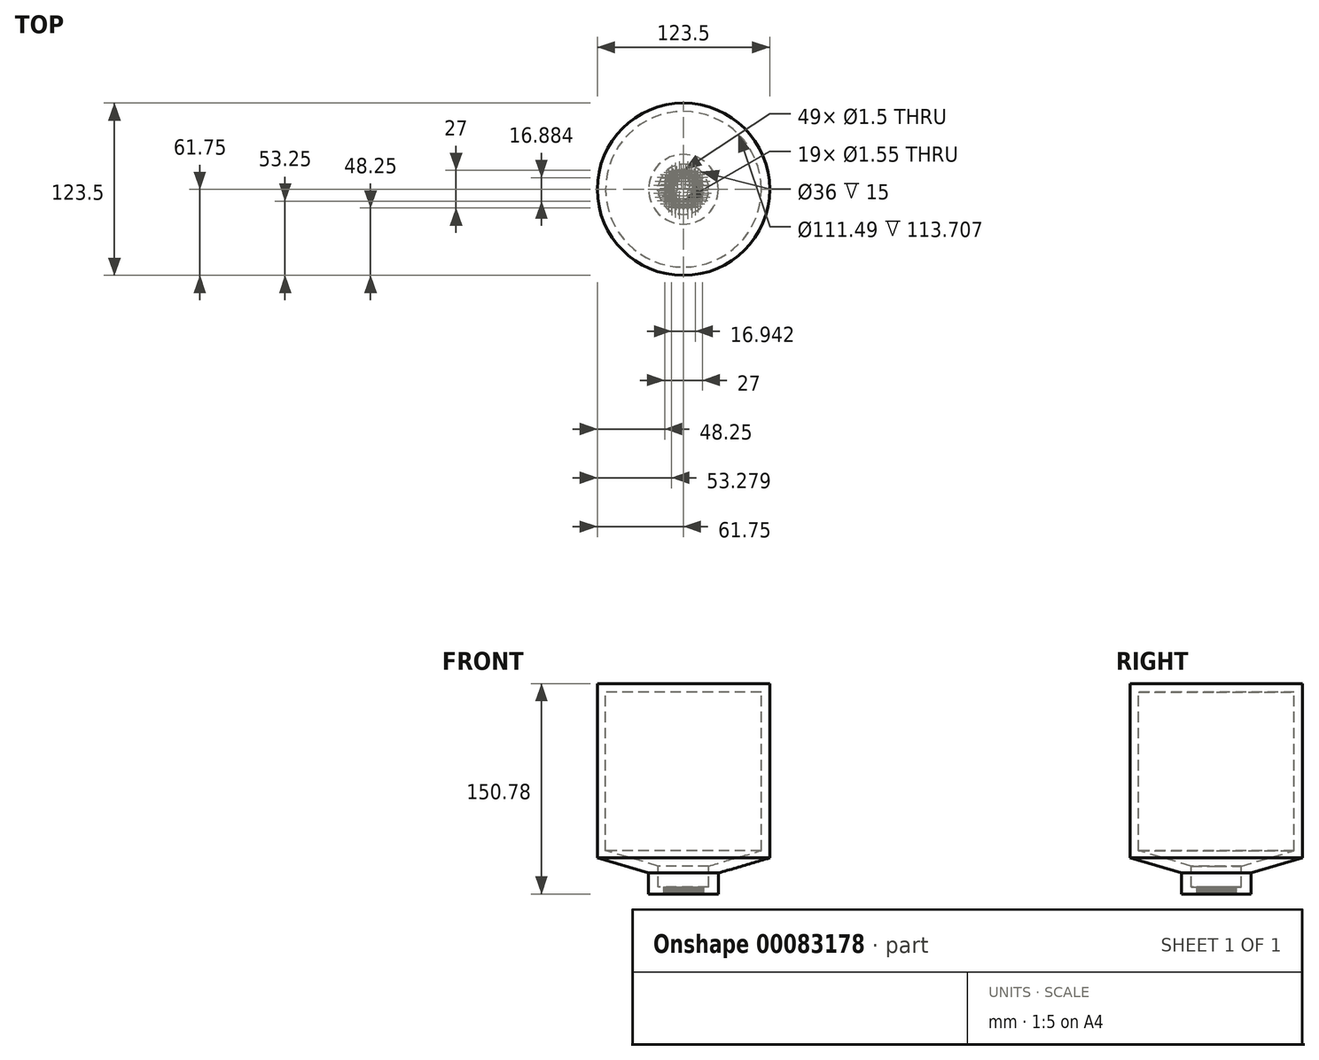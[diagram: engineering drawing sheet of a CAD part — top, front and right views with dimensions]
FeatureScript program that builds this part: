
annotation { "Feature Type Name" : "Feature", "Feature Type Description" : "" }
export const myFeature = defineFeature(function(context is Context, id is Id, definition is map)
    precondition{}
    {
        {
            var Q0;
            Q0=qCreatedBy(makeId("Front.planeOp"),FACE);
            var sketch = newSketch(context, id + "F0", { "sketchPlane" : qUnion([Q0])});
            skLineSegment(sketch, "E0", {"start": v(0, 60.78) * mm, "end": v(0, -41.7) * mm, "construction": true});
            skLineSegment(sketch, "E1", {"start": v(0, 0) * mm, "end": v(-25, 0) * mm});
            skLineSegment(sketch, "E2", {"start": v(-25, 0) * mm, "end": v(-25, 15) * mm});
            skLineSegment(sketch, "E3", {"start": v(-25, 15) * mm, "end": v(-61.75, 25.78) * mm});
            skLineSegment(sketch, "E4", {"start": v(-61.75, 25.78) * mm, "end": v(-61.75, 150.78) * mm});
            skLineSegment(sketch, "E5", {"start": v(-61.75, 150.78) * mm, "end": v(0, 150.78) * mm});
            skLineSegment(sketch, "E6", {"start": v(0, 150.78) * mm, "end": v(0, 144.78) * mm});
            skLineSegment(sketch, "E7", {"start": v(0, 144.78) * mm, "end": v(-55.75, 144.78) * mm});
            skLineSegment(sketch, "E8", {"start": v(-55.75, 144.78) * mm, "end": v(-55.75, 31.07) * mm});
            skLineSegment(sketch, "E9", {"start": v(-55.75, 31.07) * mm, "end": v(-18, 20) * mm});
            skLineSegment(sketch, "E10", {"start": v(-18, 20) * mm, "end": v(-18, 5) * mm});
            skLineSegment(sketch, "E11", {"start": v(-18, 5) * mm, "end": v(0, 5) * mm});
            skLineSegment(sketch, "E12", {"start": v(0, 0) * mm, "end": v(0, 5) * mm});
            skSolve(sketch);
        }
        {
            var Q0;
            Q0=makeQuery(id+"F0.imprint","IMPRINT",FACE,{"disambiguationData":[TD([[makeQuery(id+"F0.imprint","IMPRINT",EDGE,{"derivedFrom":sQuery(id+"F0.wireOp",EDGE,"E1")}),-1.0]])]});
            var Q1;
            Q1=sQuery(id+"F0.wireOp",EDGE,"E0");
            revolve(context, id + "F1", {"entities" : qUnion([Q0]), "axis" : qUnion([Q1]), "revolveType" : RevolveType.FULL});
        }
        {
            var Q0;
            Q0=qCreatedBy(makeId("Top.planeOp"),FACE);
            var sketch = newSketch(context, id + "F2", { "sketchPlane" : qUnion([Q0])});
            skCircle(sketch, "E13", {"center": v(0, 0) * mm, "radius": 11 * mm, "construction": true});
            skCircle(sketch, "E14", {"center": v(0, 0) * mm, "radius": 13.5 * mm, "construction": true});
            skCircle(sketch, "E15", {"center": v(0, -13.5) * mm, "radius": 0.75 * mm});
            skCircle(sketch, "E16.1.0", {"center": v(3, -13.16) * mm, "radius": 0.75 * mm});
            skCircle(sketch, "E16.2.0", {"center": v(5.86, -12.16) * mm, "radius": 0.75 * mm});
            skCircle(sketch, "E17.1.3.0", {"center": v(8.42, -10.55) * mm, "radius": 0.75 * mm});
            skCircle(sketch, "E17.1.4.0", {"center": v(10.55, -8.42) * mm, "radius": 0.75 * mm});
            skCircle(sketch, "E17.1.5.0", {"center": v(12.16, -5.86) * mm, "radius": 0.75 * mm});
            skCircle(sketch, "E17.1.6.0", {"center": v(13.16, -3) * mm, "radius": 0.75 * mm});
            skCircle(sketch, "E17.1.7.0", {"center": v(13.5, 0) * mm, "radius": 0.75 * mm});
            skCircle(sketch, "E17.1.8.0", {"center": v(13.16, 3) * mm, "radius": 0.75 * mm});
            skCircle(sketch, "E17.1.9.0", {"center": v(12.16, 5.86) * mm, "radius": 0.75 * mm});
            skCircle(sketch, "E17.1.10.0", {"center": v(10.55, 8.42) * mm, "radius": 0.75 * mm});
            skCircle(sketch, "E17.1.11.0", {"center": v(8.42, 10.55) * mm, "radius": 0.75 * mm});
            skCircle(sketch, "E17.1.12.0", {"center": v(5.86, 12.16) * mm, "radius": 0.75 * mm});
            skCircle(sketch, "E17.1.13.0", {"center": v(3, 13.16) * mm, "radius": 0.75 * mm});
            skCircle(sketch, "E17.1.14.0", {"center": v(0, 13.5) * mm, "radius": 0.75 * mm});
            skCircle(sketch, "E17.1.15.0", {"center": v(-3, 13.16) * mm, "radius": 0.75 * mm});
            skCircle(sketch, "E17.1.16.0", {"center": v(-5.86, 12.16) * mm, "radius": 0.75 * mm});
            skCircle(sketch, "E17.1.17.0", {"center": v(-8.42, 10.55) * mm, "radius": 0.75 * mm});
            skCircle(sketch, "E17.1.18.0", {"center": v(-10.55, 8.42) * mm, "radius": 0.75 * mm});
            skCircle(sketch, "E17.1.19.0", {"center": v(-12.16, 5.86) * mm, "radius": 0.75 * mm});
            skCircle(sketch, "E17.1.20.0", {"center": v(-13.16, 3) * mm, "radius": 0.75 * mm});
            skCircle(sketch, "E17.1.21.0", {"center": v(-13.5, 0) * mm, "radius": 0.75 * mm});
            skCircle(sketch, "E17.1.22.0", {"center": v(-13.16, -3) * mm, "radius": 0.75 * mm});
            skCircle(sketch, "E17.1.23.0", {"center": v(-12.16, -5.86) * mm, "radius": 0.75 * mm});
            skCircle(sketch, "E17.1.24.0", {"center": v(-10.55, -8.42) * mm, "radius": 0.75 * mm});
            skCircle(sketch, "E18.1.25.0", {"center": v(-8.42, -10.55) * mm, "radius": 0.75 * mm});
            skCircle(sketch, "E18.1.26.0", {"center": v(-5.86, -12.16) * mm, "radius": 0.75 * mm});
            skCircle(sketch, "E19.1.27.0", {"center": v(-3, -13.16) * mm, "radius": 0.75 * mm});
            skCircle(sketch, "E20", {"center": v(0, -11) * mm, "radius": 0.75 * mm});
            skCircle(sketch, "E21.1.0", {"center": v(3.24, -10.51) * mm, "radius": 0.75 * mm});
            skCircle(sketch, "E21.2.0", {"center": v(6.2, -9.09) * mm, "radius": 0.75 * mm});
            skCircle(sketch, "E21.3.0", {"center": v(8.6, -6.86) * mm, "radius": 0.75 * mm});
            skCircle(sketch, "E21.4.0", {"center": v(10.24, -4.02) * mm, "radius": 0.75 * mm});
            skCircle(sketch, "E21.5.0", {"center": v(10.97, -0.82) * mm, "radius": 0.75 * mm});
            skCircle(sketch, "E21.6.0", {"center": v(10.72, 2.45) * mm, "radius": 0.75 * mm});
            skCircle(sketch, "E21.7.0", {"center": v(9.53, 5.5) * mm, "radius": 0.75 * mm});
            skCircle(sketch, "E21.8.0", {"center": v(7.48, 8.06) * mm, "radius": 0.75 * mm});
            skCircle(sketch, "E21.9.0", {"center": v(4.77, 9.91) * mm, "radius": 0.75 * mm});
            skCircle(sketch, "E21.10.0", {"center": v(1.64, 10.88) * mm, "radius": 0.75 * mm});
            skCircle(sketch, "E21.11.0", {"center": v(-1.64, 10.88) * mm, "radius": 0.75 * mm});
            skCircle(sketch, "E21.12.0", {"center": v(-4.77, 9.91) * mm, "radius": 0.75 * mm});
            skCircle(sketch, "E21.13.0", {"center": v(-7.48, 8.06) * mm, "radius": 0.75 * mm});
            skCircle(sketch, "E21.14.0", {"center": v(-9.53, 5.5) * mm, "radius": 0.75 * mm});
            skCircle(sketch, "E21.15.0", {"center": v(-10.72, 2.45) * mm, "radius": 0.75 * mm});
            skCircle(sketch, "E21.16.0", {"center": v(-10.97, -0.82) * mm, "radius": 0.75 * mm});
            skCircle(sketch, "E21.17.0", {"center": v(-10.24, -4.02) * mm, "radius": 0.75 * mm});
            skCircle(sketch, "E21.18.0", {"center": v(-8.6, -6.86) * mm, "radius": 0.75 * mm});
            skCircle(sketch, "E21.19.0", {"center": v(-6.2, -9.09) * mm, "radius": 0.75 * mm});
            skCircle(sketch, "E21.20.0", {"center": v(-3.24, -10.51) * mm, "radius": 0.75 * mm});
            skCircle(sketch, "E22", {"center": v(0, 0) * mm, "radius": 8.5 * mm});
            skCircle(sketch, "E23", {"center": v(0, -8.5) * mm, "radius": 0.78 * mm});
            skCircle(sketch, "E24.1.0", {"center": v(2.76, -8.04) * mm, "radius": 0.78 * mm});
            skCircle(sketch, "E24.2.0", {"center": v(5.22, -6.7) * mm, "radius": 0.78 * mm});
            skCircle(sketch, "E24.3.0", {"center": v(7.12, -4.65) * mm, "radius": 0.78 * mm});
            skCircle(sketch, "E24.4.0", {"center": v(8.24, -2.09) * mm, "radius": 0.78 * mm});
            skCircle(sketch, "E24.5.0", {"center": v(8.47, 0.7) * mm, "radius": 0.78 * mm});
            skCircle(sketch, "E24.6.0", {"center": v(7.78, 3.41) * mm, "radius": 0.78 * mm});
            skCircle(sketch, "E24.7.0", {"center": v(6.25, 5.76) * mm, "radius": 0.78 * mm});
            skCircle(sketch, "E24.8.0", {"center": v(4.05, 7.48) * mm, "radius": 0.78 * mm});
            skCircle(sketch, "E24.9.0", {"center": v(1.4, 8.38) * mm, "radius": 0.78 * mm});
            skCircle(sketch, "E24.10.0", {"center": v(-1.4, 8.38) * mm, "radius": 0.78 * mm});
            skCircle(sketch, "E24.11.0", {"center": v(-4.05, 7.48) * mm, "radius": 0.78 * mm});
            skCircle(sketch, "E24.12.0", {"center": v(-6.25, 5.76) * mm, "radius": 0.78 * mm});
            skCircle(sketch, "E24.13.0", {"center": v(-7.78, 3.41) * mm, "radius": 0.78 * mm});
            skCircle(sketch, "E24.14.0", {"center": v(-8.47, 0.7) * mm, "radius": 0.78 * mm});
            skCircle(sketch, "E24.15.0", {"center": v(-8.24, -2.09) * mm, "radius": 0.78 * mm});
            skCircle(sketch, "E24.16.0", {"center": v(-7.12, -4.65) * mm, "radius": 0.78 * mm});
            skCircle(sketch, "E24.17.0", {"center": v(-5.22, -6.7) * mm, "radius": 0.78 * mm});
            skCircle(sketch, "E24.18.0", {"center": v(-2.76, -8.04) * mm, "radius": 0.78 * mm});
            skSolve(sketch);
        }
        {
            var Q0;
            Q0=makeQuery(id+"F2.imprint","IMPRINT",FACE,{"disambiguationData":[TD([[makeQuery(id+"F2.imprint","IMPRINT",EDGE,{"derivedFrom":sQuery(id+"F2.wireOp",EDGE,"E17.1.13.0")}),1.0]])]});
            var Q1;
            Q1=makeQuery(id+"F2.imprint","IMPRINT",FACE,{"disambiguationData":[TD([[makeQuery(id+"F2.imprint","IMPRINT",EDGE,{"derivedFrom":sQuery(id+"F2.wireOp",EDGE,"E17.1.14.0")}),1.0]])]});
            var Q2;
            Q2=makeQuery(id+"F2.imprint","IMPRINT",FACE,{"disambiguationData":[TD([[makeQuery(id+"F2.imprint","IMPRINT",EDGE,{"derivedFrom":sQuery(id+"F2.wireOp",EDGE,"E17.1.4.0")}),1.0]])]});
            var Q3;
            Q3=makeQuery(id+"F2.imprint","IMPRINT",FACE,{"disambiguationData":[TD([[makeQuery(id+"F2.imprint","IMPRINT",EDGE,{"derivedFrom":sQuery(id+"F2.wireOp",EDGE,"E17.1.5.0")}),1.0]])]});
            var Q4;
            Q4=makeQuery(id+"F2.imprint","IMPRINT",FACE,{"disambiguationData":[TD([[makeQuery(id+"F2.imprint","IMPRINT",EDGE,{"derivedFrom":sQuery(id+"F2.wireOp",EDGE,"E17.1.6.0")}),1.0]])]});
            var Q5;
            {var subQ0=sQuery(id+"F2.wireOp",EDGE,"E24.18.0");var subQ1=sQuery(id+"F2.wireOp",EDGE,"E22");var subQ2=makeQuery(id+"F2.imprint","INTERSECT",VERTEX,{"disambiguationData":[OD(0.0)],"derivedFrom":[subQ1,subQ0]});Q5=makeQuery(id+"F2.imprint","IMPRINT",FACE,{"disambiguationData":[TD([[makeQuery(id+"F2.imprint","IMPRINT",EDGE,{"disambiguationData":[TD([[subQ2,-1.0]])],"derivedFrom":subQ1}),1.0]])]});}
            var Q6;
            Q6=makeQuery(id+"F2.imprint","IMPRINT",FACE,{"disambiguationData":[TD([[makeQuery(id+"F2.imprint","IMPRINT",EDGE,{"derivedFrom":sQuery(id+"F2.wireOp",EDGE,"E21.11.0")}),1.0]])]});
            var Q7;
            Q7=makeQuery(id+"F2.imprint","IMPRINT",FACE,{"disambiguationData":[TD([[makeQuery(id+"F2.imprint","IMPRINT",EDGE,{"derivedFrom":sQuery(id+"F2.wireOp",EDGE,"E17.1.10.0")}),1.0]])]});
            var Q8;
            Q8=makeQuery(id+"F2.imprint","IMPRINT",FACE,{"disambiguationData":[TD([[makeQuery(id+"F2.imprint","IMPRINT",EDGE,{"derivedFrom":sQuery(id+"F2.wireOp",EDGE,"E17.1.9.0")}),1.0]])]});
            var Q9;
            Q9=makeQuery(id+"F2.imprint","IMPRINT",FACE,{"disambiguationData":[TD([[makeQuery(id+"F2.imprint","IMPRINT",EDGE,{"derivedFrom":sQuery(id+"F2.wireOp",EDGE,"E21.5.0")}),1.0]])]});
            var Q10;
            Q10=makeQuery(id+"F2.imprint","IMPRINT",FACE,{"disambiguationData":[TD([[makeQuery(id+"F2.imprint","IMPRINT",EDGE,{"derivedFrom":sQuery(id+"F2.wireOp",EDGE,"E17.1.11.0")}),1.0]])]});
            var Q11;
            Q11=makeQuery(id+"F2.imprint","IMPRINT",FACE,{"disambiguationData":[TD([[makeQuery(id+"F2.imprint","IMPRINT",EDGE,{"derivedFrom":sQuery(id+"F2.wireOp",EDGE,"E21.13.0")}),1.0]])]});
            var Q12;
            Q12=makeQuery(id+"F2.imprint","IMPRINT",FACE,{"disambiguationData":[TD([[makeQuery(id+"F2.imprint","IMPRINT",EDGE,{"derivedFrom":sQuery(id+"F2.wireOp",EDGE,"E17.1.12.0")}),1.0]])]});
            var Q13;
            Q13=makeQuery(id+"F2.imprint","IMPRINT",FACE,{"disambiguationData":[TD([[makeQuery(id+"F2.imprint","IMPRINT",EDGE,{"derivedFrom":sQuery(id+"F2.wireOp",EDGE,"E21.6.0")}),1.0]])]});
            var Q14;
            {var subQ0=sQuery(id+"F2.wireOp",EDGE,"E24.11.0");var subQ1=sQuery(id+"F2.wireOp",EDGE,"E22");var subQ2=makeQuery(id+"F2.imprint","INTERSECT",VERTEX,{"disambiguationData":[OD(0.0)],"derivedFrom":[subQ1,subQ0]});Q14=makeQuery(id+"F2.imprint","IMPRINT",FACE,{"disambiguationData":[TD([[makeQuery(id+"F2.imprint","IMPRINT",EDGE,{"disambiguationData":[TD([[subQ2,-1.0]])],"derivedFrom":subQ1}),-1.0]])]});}
            var Q15;
            Q15=makeQuery(id+"F2.imprint","IMPRINT",FACE,{"disambiguationData":[TD([[makeQuery(id+"F2.imprint","IMPRINT",EDGE,{"derivedFrom":sQuery(id+"F2.wireOp",EDGE,"E21.10.0")}),1.0]])]});
            var Q16;
            Q16=makeQuery(id+"F2.imprint","IMPRINT",FACE,{"disambiguationData":[TD([[makeQuery(id+"F2.imprint","IMPRINT",EDGE,{"derivedFrom":sQuery(id+"F2.wireOp",EDGE,"E16.1.0")}),1.0]])]});
            var Q17;
            Q17=makeQuery(id+"F2.imprint","IMPRINT",FACE,{"disambiguationData":[TD([[makeQuery(id+"F2.imprint","IMPRINT",EDGE,{"derivedFrom":sQuery(id+"F2.wireOp",EDGE,"E17.1.22.0")}),1.0]])]});
            var Q18;
            Q18=makeQuery(id+"F2.imprint","IMPRINT",FACE,{"disambiguationData":[TD([[makeQuery(id+"F2.imprint","IMPRINT",EDGE,{"derivedFrom":sQuery(id+"F2.wireOp",EDGE,"E21.7.0")}),1.0]])]});
            var Q19;
            Q19=makeQuery(id+"F2.imprint","IMPRINT",FACE,{"disambiguationData":[TD([[makeQuery(id+"F2.imprint","IMPRINT",EDGE,{"derivedFrom":sQuery(id+"F2.wireOp",EDGE,"E17.1.19.0")}),1.0]])]});
            var Q20;
            {var subQ0=sQuery(id+"F2.wireOp",EDGE,"E24.2.0");var subQ1=sQuery(id+"F2.wireOp",EDGE,"E22");var subQ2=makeQuery(id+"F2.imprint","INTERSECT",VERTEX,{"disambiguationData":[OD(0.0)],"derivedFrom":[subQ1,subQ0]});Q20=makeQuery(id+"F2.imprint","IMPRINT",FACE,{"disambiguationData":[TD([[makeQuery(id+"F2.imprint","IMPRINT",EDGE,{"disambiguationData":[TD([[subQ2,-1.0]])],"derivedFrom":subQ1}),1.0]])]});}
            var Q21;
            {var subQ0=sQuery(id+"F2.wireOp",EDGE,"E24.8.0");var subQ1=sQuery(id+"F2.wireOp",EDGE,"E22");var subQ2=makeQuery(id+"F2.imprint","INTERSECT",VERTEX,{"disambiguationData":[OD(0.0)],"derivedFrom":[subQ1,subQ0]});Q21=makeQuery(id+"F2.imprint","IMPRINT",FACE,{"disambiguationData":[TD([[makeQuery(id+"F2.imprint","IMPRINT",EDGE,{"disambiguationData":[TD([[subQ2,-1.0]])],"derivedFrom":subQ1}),-1.0]])]});}
            var Q22;
            Q22=makeQuery(id+"F2.imprint","IMPRINT",FACE,{"disambiguationData":[TD([[makeQuery(id+"F2.imprint","IMPRINT",EDGE,{"derivedFrom":sQuery(id+"F2.wireOp",EDGE,"E21.14.0")}),1.0]])]});
            var Q23;
            Q23=makeQuery(id+"F2.imprint","IMPRINT",FACE,{"disambiguationData":[TD([[makeQuery(id+"F2.imprint","IMPRINT",EDGE,{"derivedFrom":sQuery(id+"F2.wireOp",EDGE,"E17.1.20.0")}),1.0]])]});
            var Q24;
            {var subQ0=sQuery(id+"F2.wireOp",EDGE,"E24.15.0");var subQ1=sQuery(id+"F2.wireOp",EDGE,"E22");var subQ2=makeQuery(id+"F2.imprint","INTERSECT",VERTEX,{"disambiguationData":[OD(0.0)],"derivedFrom":[subQ1,subQ0]});Q24=makeQuery(id+"F2.imprint","IMPRINT",FACE,{"disambiguationData":[TD([[makeQuery(id+"F2.imprint","IMPRINT",EDGE,{"disambiguationData":[TD([[subQ2,-1.0]])],"derivedFrom":subQ1}),1.0]])]});}
            var Q25;
            Q25=makeQuery(id+"F2.imprint","IMPRINT",FACE,{"disambiguationData":[TD([[makeQuery(id+"F2.imprint","IMPRINT",EDGE,{"derivedFrom":sQuery(id+"F2.wireOp",EDGE,"E20")}),1.0]])]});
            var Q26;
            {var subQ0=sQuery(id+"F2.wireOp",EDGE,"E24.10.0");var subQ1=sQuery(id+"F2.wireOp",EDGE,"E22");var subQ2=makeQuery(id+"F2.imprint","INTERSECT",VERTEX,{"disambiguationData":[OD(0.0)],"derivedFrom":[subQ1,subQ0]});Q26=makeQuery(id+"F2.imprint","IMPRINT",FACE,{"disambiguationData":[TD([[makeQuery(id+"F2.imprint","IMPRINT",EDGE,{"disambiguationData":[TD([[subQ2,-1.0]])],"derivedFrom":subQ1}),-1.0]])]});}
            var Q27;
            {var subQ0=sQuery(id+"F2.wireOp",EDGE,"E24.4.0");var subQ1=sQuery(id+"F2.wireOp",EDGE,"E22");var subQ2=makeQuery(id+"F2.imprint","INTERSECT",VERTEX,{"disambiguationData":[OD(0.0)],"derivedFrom":[subQ1,subQ0]});Q27=makeQuery(id+"F2.imprint","IMPRINT",FACE,{"disambiguationData":[TD([[makeQuery(id+"F2.imprint","IMPRINT",EDGE,{"disambiguationData":[TD([[subQ2,-1.0]])],"derivedFrom":subQ1}),1.0]])]});}
            var Q28;
            Q28=makeQuery(id+"F2.imprint","IMPRINT",FACE,{"disambiguationData":[TD([[makeQuery(id+"F2.imprint","IMPRINT",EDGE,{"derivedFrom":sQuery(id+"F2.wireOp",EDGE,"E21.2.0")}),1.0]])]});
            var Q29;
            Q29=makeQuery(id+"F2.imprint","IMPRINT",FACE,{"disambiguationData":[TD([[makeQuery(id+"F2.imprint","IMPRINT",EDGE,{"derivedFrom":sQuery(id+"F2.wireOp",EDGE,"E21.9.0")}),1.0]])]});
            var Q30;
            Q30=makeQuery(id+"F2.imprint","IMPRINT",FACE,{"disambiguationData":[TD([[makeQuery(id+"F2.imprint","IMPRINT",EDGE,{"derivedFrom":sQuery(id+"F2.wireOp",EDGE,"E21.15.0")}),1.0]])]});
            var Q31;
            Q31=makeQuery(id+"F1.opRevolve","SWEPT_FACE",FACE,{"disambiguationData":[OSD([sQuery(id+"F0.wireOp",EDGE,"E11")])]});
            var Q32;
            Q32=makeQuery(id+"F2.imprint","IMPRINT",FACE,{"disambiguationData":[TD([[makeQuery(id+"F2.imprint","IMPRINT",EDGE,{"derivedFrom":sQuery(id+"F2.wireOp",EDGE,"E17.1.3.0")}),1.0]])]});
            var Q33;
            {var subQ0=sQuery(id+"F2.wireOp",EDGE,"E24.18.0");var subQ1=sQuery(id+"F2.wireOp",EDGE,"E22");var subQ2=makeQuery(id+"F2.imprint","INTERSECT",VERTEX,{"disambiguationData":[OD(0.0)],"derivedFrom":[subQ1,subQ0]});Q33=makeQuery(id+"F2.imprint","IMPRINT",FACE,{"disambiguationData":[TD([[makeQuery(id+"F2.imprint","IMPRINT",EDGE,{"disambiguationData":[TD([[subQ2,-1.0]])],"derivedFrom":subQ1}),-1.0]])]});}
            var Q34;
            Q34=makeQuery(id+"F2.imprint","IMPRINT",FACE,{"disambiguationData":[TD([[makeQuery(id+"F2.imprint","IMPRINT",EDGE,{"derivedFrom":sQuery(id+"F2.wireOp",EDGE,"E17.1.18.0")}),1.0]])]});
            var Q35;
            Q35=makeQuery(id+"F2.imprint","IMPRINT",FACE,{"disambiguationData":[TD([[makeQuery(id+"F2.imprint","IMPRINT",EDGE,{"derivedFrom":sQuery(id+"F2.wireOp",EDGE,"E16.2.0")}),1.0]])]});
            var Q36;
            Q36=makeQuery(id+"F2.imprint","IMPRINT",FACE,{"disambiguationData":[TD([[makeQuery(id+"F2.imprint","IMPRINT",EDGE,{"derivedFrom":sQuery(id+"F2.wireOp",EDGE,"E17.1.16.0")}),1.0]])]});
            var Q37;
            Q37=makeQuery(id+"F2.imprint","IMPRINT",FACE,{"disambiguationData":[TD([[makeQuery(id+"F2.imprint","IMPRINT",EDGE,{"derivedFrom":sQuery(id+"F2.wireOp",EDGE,"E17.1.7.0")}),1.0]])]});
            var Q38;
            Q38=makeQuery(id+"F2.imprint","IMPRINT",FACE,{"disambiguationData":[TD([[makeQuery(id+"F2.imprint","IMPRINT",EDGE,{"derivedFrom":sQuery(id+"F2.wireOp",EDGE,"E17.1.8.0")}),1.0]])]});
            var Q39;
            {var subQ0=sQuery(id+"F2.wireOp",EDGE,"E24.12.0");var subQ1=sQuery(id+"F2.wireOp",EDGE,"E22");var subQ2=makeQuery(id+"F2.imprint","INTERSECT",VERTEX,{"disambiguationData":[OD(0.0)],"derivedFrom":[subQ1,subQ0]});Q39=makeQuery(id+"F2.imprint","IMPRINT",FACE,{"disambiguationData":[TD([[makeQuery(id+"F2.imprint","IMPRINT",EDGE,{"disambiguationData":[TD([[subQ2,-1.0]])],"derivedFrom":subQ1}),-1.0]])]});}
            var Q40;
            Q40=makeQuery(id+"F2.imprint","IMPRINT",FACE,{"disambiguationData":[TD([[makeQuery(id+"F2.imprint","IMPRINT",EDGE,{"derivedFrom":sQuery(id+"F2.wireOp",EDGE,"E17.1.23.0")}),1.0]])]});
            var Q41;
            {var subQ0=sQuery(id+"F2.wireOp",EDGE,"E24.6.0");var subQ1=sQuery(id+"F2.wireOp",EDGE,"E22");var subQ2=makeQuery(id+"F2.imprint","INTERSECT",VERTEX,{"disambiguationData":[OD(0.0)],"derivedFrom":[subQ1,subQ0]});Q41=makeQuery(id+"F2.imprint","IMPRINT",FACE,{"disambiguationData":[TD([[makeQuery(id+"F2.imprint","IMPRINT",EDGE,{"disambiguationData":[TD([[subQ2,-1.0]])],"derivedFrom":subQ1}),1.0]])]});}
            var Q42;
            Q42=makeQuery(id+"F2.imprint","IMPRINT",FACE,{"disambiguationData":[TD([[makeQuery(id+"F2.imprint","IMPRINT",EDGE,{"derivedFrom":sQuery(id+"F2.wireOp",EDGE,"E17.1.17.0")}),1.0]])]});
            var Q43;
            {var subQ0=sQuery(id+"F2.wireOp",EDGE,"E23");var subQ1=sQuery(id+"F2.wireOp",EDGE,"E22");var subQ2=makeQuery(id+"F2.imprint","INTERSECT",VERTEX,{"disambiguationData":[OD(0.0)],"derivedFrom":[subQ1,subQ0]});Q43=makeQuery(id+"F2.imprint","IMPRINT",FACE,{"disambiguationData":[TD([[makeQuery(id+"F2.imprint","IMPRINT",EDGE,{"disambiguationData":[TD([[subQ2,-1.0]])],"derivedFrom":subQ1}),1.0]])]});}
            var Q44;
            Q44=makeQuery(id+"F2.imprint","IMPRINT",FACE,{"disambiguationData":[TD([[makeQuery(id+"F2.imprint","IMPRINT",EDGE,{"derivedFrom":sQuery(id+"F2.wireOp",EDGE,"E21.19.0")}),1.0]])]});
            var Q45;
            {var subQ0=sQuery(id+"F2.wireOp",EDGE,"E24.11.0");var subQ1=sQuery(id+"F2.wireOp",EDGE,"E22");var subQ2=makeQuery(id+"F2.imprint","INTERSECT",VERTEX,{"disambiguationData":[OD(0.0)],"derivedFrom":[subQ1,subQ0]});Q45=makeQuery(id+"F2.imprint","IMPRINT",FACE,{"disambiguationData":[TD([[makeQuery(id+"F2.imprint","IMPRINT",EDGE,{"disambiguationData":[TD([[subQ2,-1.0]])],"derivedFrom":subQ1}),1.0]])]});}
            var Q46;
            Q46=makeQuery(id+"F2.imprint","IMPRINT",FACE,{"disambiguationData":[TD([[makeQuery(id+"F2.imprint","IMPRINT",EDGE,{"derivedFrom":sQuery(id+"F2.wireOp",EDGE,"E21.3.0")}),1.0]])]});
            var Q47;
            {var subQ0=sQuery(id+"F2.wireOp",EDGE,"E24.14.0");var subQ1=sQuery(id+"F2.wireOp",EDGE,"E22");var subQ2=makeQuery(id+"F2.imprint","INTERSECT",VERTEX,{"disambiguationData":[OD(0.0)],"derivedFrom":[subQ1,subQ0]});Q47=makeQuery(id+"F2.imprint","IMPRINT",FACE,{"disambiguationData":[TD([[makeQuery(id+"F2.imprint","IMPRINT",EDGE,{"disambiguationData":[TD([[subQ2,-1.0]])],"derivedFrom":subQ1}),-1.0]])]});}
            var Q48;
            Q48=makeQuery(id+"F2.imprint","IMPRINT",FACE,{"disambiguationData":[TD([[makeQuery(id+"F2.imprint","IMPRINT",EDGE,{"derivedFrom":sQuery(id+"F2.wireOp",EDGE,"E18.1.25.0")}),1.0]])]});
            var Q49;
            {var subQ0=sQuery(id+"F2.wireOp",EDGE,"E24.3.0");var subQ1=sQuery(id+"F2.wireOp",EDGE,"E22");var subQ2=makeQuery(id+"F2.imprint","INTERSECT",VERTEX,{"disambiguationData":[OD(0.0)],"derivedFrom":[subQ1,subQ0]});Q49=makeQuery(id+"F2.imprint","IMPRINT",FACE,{"disambiguationData":[TD([[makeQuery(id+"F2.imprint","IMPRINT",EDGE,{"disambiguationData":[TD([[subQ2,-1.0]])],"derivedFrom":subQ1}),-1.0]])]});}
            var Q50;
            {var subQ0=sQuery(id+"F2.wireOp",EDGE,"E24.10.0");var subQ1=sQuery(id+"F2.wireOp",EDGE,"E22");var subQ2=makeQuery(id+"F2.imprint","INTERSECT",VERTEX,{"disambiguationData":[OD(0.0)],"derivedFrom":[subQ1,subQ0]});Q50=makeQuery(id+"F2.imprint","IMPRINT",FACE,{"disambiguationData":[TD([[makeQuery(id+"F2.imprint","IMPRINT",EDGE,{"disambiguationData":[TD([[subQ2,-1.0]])],"derivedFrom":subQ1}),1.0]])]});}
            var Q51;
            {var subQ0=sQuery(id+"F2.wireOp",EDGE,"E24.6.0");var subQ1=sQuery(id+"F2.wireOp",EDGE,"E22");var subQ2=makeQuery(id+"F2.imprint","INTERSECT",VERTEX,{"disambiguationData":[OD(0.0)],"derivedFrom":[subQ1,subQ0]});Q51=makeQuery(id+"F2.imprint","IMPRINT",FACE,{"disambiguationData":[TD([[makeQuery(id+"F2.imprint","IMPRINT",EDGE,{"disambiguationData":[TD([[subQ2,-1.0]])],"derivedFrom":subQ1}),-1.0]])]});}
            var Q52;
            {var subQ0=sQuery(id+"F2.wireOp",EDGE,"E24.17.0");var subQ1=sQuery(id+"F2.wireOp",EDGE,"E22");var subQ2=makeQuery(id+"F2.imprint","INTERSECT",VERTEX,{"disambiguationData":[OD(0.0)],"derivedFrom":[subQ1,subQ0]});Q52=makeQuery(id+"F2.imprint","IMPRINT",FACE,{"disambiguationData":[TD([[makeQuery(id+"F2.imprint","IMPRINT",EDGE,{"disambiguationData":[TD([[subQ2,-1.0]])],"derivedFrom":subQ1}),1.0]])]});}
            var Q53;
            {var subQ0=sQuery(id+"F2.wireOp",EDGE,"E24.1.0");var subQ1=sQuery(id+"F2.wireOp",EDGE,"E22");var subQ2=makeQuery(id+"F2.imprint","INTERSECT",VERTEX,{"disambiguationData":[OD(0.0)],"derivedFrom":[subQ1,subQ0]});Q53=makeQuery(id+"F2.imprint","IMPRINT",FACE,{"disambiguationData":[TD([[makeQuery(id+"F2.imprint","IMPRINT",EDGE,{"disambiguationData":[TD([[subQ2,-1.0]])],"derivedFrom":subQ1}),-1.0]])]});}
            var Q54;
            Q54=makeQuery(id+"F2.imprint","IMPRINT",FACE,{"disambiguationData":[TD([[makeQuery(id+"F2.imprint","IMPRINT",EDGE,{"derivedFrom":sQuery(id+"F2.wireOp",EDGE,"E17.1.15.0")}),1.0]])]});
            var Q55;
            {var subQ0=sQuery(id+"F2.wireOp",EDGE,"E24.9.0");var subQ1=sQuery(id+"F2.wireOp",EDGE,"E22");var subQ2=makeQuery(id+"F2.imprint","INTERSECT",VERTEX,{"disambiguationData":[OD(0.0)],"derivedFrom":[subQ1,subQ0]});Q55=makeQuery(id+"F2.imprint","IMPRINT",FACE,{"disambiguationData":[TD([[makeQuery(id+"F2.imprint","IMPRINT",EDGE,{"disambiguationData":[TD([[subQ2,-1.0]])],"derivedFrom":subQ1}),1.0]])]});}
            var Q56;
            Q56=makeQuery(id+"F2.imprint","IMPRINT",FACE,{"disambiguationData":[TD([[makeQuery(id+"F2.imprint","IMPRINT",EDGE,{"derivedFrom":sQuery(id+"F2.wireOp",EDGE,"E21.20.0")}),1.0]])]});
            var Q57;
            Q57=makeQuery(id+"F2.imprint","IMPRINT",FACE,{"disambiguationData":[TD([[makeQuery(id+"F2.imprint","IMPRINT",EDGE,{"derivedFrom":sQuery(id+"F2.wireOp",EDGE,"E21.4.0")}),1.0]])]});
            var Q58;
            {var subQ0=sQuery(id+"F2.wireOp",EDGE,"E24.7.0");var subQ1=sQuery(id+"F2.wireOp",EDGE,"E22");var subQ2=makeQuery(id+"F2.imprint","INTERSECT",VERTEX,{"disambiguationData":[OD(0.0)],"derivedFrom":[subQ1,subQ0]});Q58=makeQuery(id+"F2.imprint","IMPRINT",FACE,{"disambiguationData":[TD([[makeQuery(id+"F2.imprint","IMPRINT",EDGE,{"disambiguationData":[TD([[subQ2,-1.0]])],"derivedFrom":subQ1}),-1.0]])]});}
            var Q59;
            {var subQ0=sQuery(id+"F2.wireOp",EDGE,"E24.2.0");var subQ1=sQuery(id+"F2.wireOp",EDGE,"E22");var subQ2=makeQuery(id+"F2.imprint","INTERSECT",VERTEX,{"disambiguationData":[OD(0.0)],"derivedFrom":[subQ1,subQ0]});Q59=makeQuery(id+"F2.imprint","IMPRINT",FACE,{"disambiguationData":[TD([[makeQuery(id+"F2.imprint","IMPRINT",EDGE,{"disambiguationData":[TD([[subQ2,-1.0]])],"derivedFrom":subQ1}),-1.0]])]});}
            var Q60;
            {var subQ0=sQuery(id+"F2.wireOp",EDGE,"E24.4.0");var subQ1=sQuery(id+"F2.wireOp",EDGE,"E22");var subQ2=makeQuery(id+"F2.imprint","INTERSECT",VERTEX,{"disambiguationData":[OD(0.0)],"derivedFrom":[subQ1,subQ0]});Q60=makeQuery(id+"F2.imprint","IMPRINT",FACE,{"disambiguationData":[TD([[makeQuery(id+"F2.imprint","IMPRINT",EDGE,{"disambiguationData":[TD([[subQ2,-1.0]])],"derivedFrom":subQ1}),-1.0]])]});}
            var Q61;
            Q61=makeQuery(id+"F2.imprint","IMPRINT",FACE,{"disambiguationData":[TD([[makeQuery(id+"F2.imprint","IMPRINT",EDGE,{"derivedFrom":sQuery(id+"F2.wireOp",EDGE,"E15")}),1.0]])]});
            var Q62;
            Q62=makeQuery(id+"F2.imprint","IMPRINT",FACE,{"disambiguationData":[TD([[makeQuery(id+"F2.imprint","IMPRINT",EDGE,{"derivedFrom":sQuery(id+"F2.wireOp",EDGE,"E17.1.24.0")}),1.0]])]});
            var Q63;
            {var subQ0=sQuery(id+"F2.wireOp",EDGE,"E24.13.0");var subQ1=sQuery(id+"F2.wireOp",EDGE,"E22");var subQ2=makeQuery(id+"F2.imprint","INTERSECT",VERTEX,{"disambiguationData":[OD(0.0)],"derivedFrom":[subQ1,subQ0]});Q63=makeQuery(id+"F2.imprint","IMPRINT",FACE,{"disambiguationData":[TD([[makeQuery(id+"F2.imprint","IMPRINT",EDGE,{"disambiguationData":[TD([[subQ2,-1.0]])],"derivedFrom":subQ1}),-1.0]])]});}
            var Q64;
            {var subQ0=sQuery(id+"F2.wireOp",EDGE,"E24.1.0");var subQ1=sQuery(id+"F2.wireOp",EDGE,"E22");var subQ2=makeQuery(id+"F2.imprint","INTERSECT",VERTEX,{"disambiguationData":[OD(0.0)],"derivedFrom":[subQ1,subQ0]});Q64=makeQuery(id+"F2.imprint","IMPRINT",FACE,{"disambiguationData":[TD([[makeQuery(id+"F2.imprint","IMPRINT",EDGE,{"disambiguationData":[TD([[subQ2,-1.0]])],"derivedFrom":subQ1}),1.0]])]});}
            var Q65;
            {var subQ0=sQuery(id+"F2.wireOp",EDGE,"E24.5.0");var subQ1=sQuery(id+"F2.wireOp",EDGE,"E22");var subQ2=makeQuery(id+"F2.imprint","INTERSECT",VERTEX,{"disambiguationData":[OD(0.0)],"derivedFrom":[subQ1,subQ0]});Q65=makeQuery(id+"F2.imprint","IMPRINT",FACE,{"disambiguationData":[TD([[makeQuery(id+"F2.imprint","IMPRINT",EDGE,{"disambiguationData":[TD([[subQ2,1.0]])],"derivedFrom":subQ1}),1.0]])]});}
            var Q66;
            Q66=makeQuery(id+"F2.imprint","IMPRINT",FACE,{"disambiguationData":[TD([[makeQuery(id+"F2.imprint","IMPRINT",EDGE,{"derivedFrom":sQuery(id+"F2.wireOp",EDGE,"E21.12.0")}),1.0]])]});
            var Q67;
            {var subQ0=sQuery(id+"F2.wireOp",EDGE,"E24.5.0");var subQ1=sQuery(id+"F2.wireOp",EDGE,"E22");var subQ2=makeQuery(id+"F2.imprint","INTERSECT",VERTEX,{"disambiguationData":[OD(0.0)],"derivedFrom":[subQ1,subQ0]});Q67=makeQuery(id+"F2.imprint","IMPRINT",FACE,{"disambiguationData":[TD([[makeQuery(id+"F2.imprint","IMPRINT",EDGE,{"disambiguationData":[TD([[subQ2,1.0]])],"derivedFrom":subQ1}),-1.0]])]});}
            var Q68;
            {var subQ0=sQuery(id+"F2.wireOp",EDGE,"E24.12.0");var subQ1=sQuery(id+"F2.wireOp",EDGE,"E22");var subQ2=makeQuery(id+"F2.imprint","INTERSECT",VERTEX,{"disambiguationData":[OD(0.0)],"derivedFrom":[subQ1,subQ0]});Q68=makeQuery(id+"F2.imprint","IMPRINT",FACE,{"disambiguationData":[TD([[makeQuery(id+"F2.imprint","IMPRINT",EDGE,{"disambiguationData":[TD([[subQ2,-1.0]])],"derivedFrom":subQ1}),1.0]])]});}
            var Q69;
            Q69=makeQuery(id+"F2.imprint","IMPRINT",FACE,{"disambiguationData":[TD([[makeQuery(id+"F2.imprint","IMPRINT",EDGE,{"derivedFrom":sQuery(id+"F2.wireOp",EDGE,"E21.17.0")}),1.0]])]});
            var Q70;
            {var subQ0=sQuery(id+"F2.wireOp",EDGE,"E24.15.0");var subQ1=sQuery(id+"F2.wireOp",EDGE,"E22");var subQ2=makeQuery(id+"F2.imprint","INTERSECT",VERTEX,{"disambiguationData":[OD(0.0)],"derivedFrom":[subQ1,subQ0]});Q70=makeQuery(id+"F2.imprint","IMPRINT",FACE,{"disambiguationData":[TD([[makeQuery(id+"F2.imprint","IMPRINT",EDGE,{"disambiguationData":[TD([[subQ2,-1.0]])],"derivedFrom":subQ1}),-1.0]])]});}
            var Q71;
            Q71=makeQuery(id+"F2.imprint","IMPRINT",FACE,{"disambiguationData":[TD([[makeQuery(id+"F2.imprint","IMPRINT",EDGE,{"derivedFrom":sQuery(id+"F2.wireOp",EDGE,"E18.1.26.0")}),1.0]])]});
            var Q72;
            Q72=makeQuery(id+"F2.imprint","IMPRINT",FACE,{"disambiguationData":[TD([[makeQuery(id+"F2.imprint","IMPRINT",EDGE,{"derivedFrom":sQuery(id+"F2.wireOp",EDGE,"E21.8.0")}),1.0]])]});
            var Q73;
            Q73=makeQuery(id+"F2.imprint","IMPRINT",FACE,{"disambiguationData":[TD([[makeQuery(id+"F2.imprint","IMPRINT",EDGE,{"derivedFrom":sQuery(id+"F2.wireOp",EDGE,"E21.1.0")}),1.0]])]});
            var Q74;
            {var subQ0=sQuery(id+"F2.wireOp",EDGE,"E24.9.0");var subQ1=sQuery(id+"F2.wireOp",EDGE,"E22");var subQ2=makeQuery(id+"F2.imprint","INTERSECT",VERTEX,{"disambiguationData":[OD(0.0)],"derivedFrom":[subQ1,subQ0]});Q74=makeQuery(id+"F2.imprint","IMPRINT",FACE,{"disambiguationData":[TD([[makeQuery(id+"F2.imprint","IMPRINT",EDGE,{"disambiguationData":[TD([[subQ2,-1.0]])],"derivedFrom":subQ1}),-1.0]])]});}
            var Q75;
            {var subQ0=sQuery(id+"F2.wireOp",EDGE,"E24.3.0");var subQ1=sQuery(id+"F2.wireOp",EDGE,"E22");var subQ2=makeQuery(id+"F2.imprint","INTERSECT",VERTEX,{"disambiguationData":[OD(0.0)],"derivedFrom":[subQ1,subQ0]});Q75=makeQuery(id+"F2.imprint","IMPRINT",FACE,{"disambiguationData":[TD([[makeQuery(id+"F2.imprint","IMPRINT",EDGE,{"disambiguationData":[TD([[subQ2,-1.0]])],"derivedFrom":subQ1}),1.0]])]});}
            var Q76;
            {var subQ0=sQuery(id+"F2.wireOp",EDGE,"E24.8.0");var subQ1=sQuery(id+"F2.wireOp",EDGE,"E22");var subQ2=makeQuery(id+"F2.imprint","INTERSECT",VERTEX,{"disambiguationData":[OD(0.0)],"derivedFrom":[subQ1,subQ0]});Q76=makeQuery(id+"F2.imprint","IMPRINT",FACE,{"disambiguationData":[TD([[makeQuery(id+"F2.imprint","IMPRINT",EDGE,{"disambiguationData":[TD([[subQ2,-1.0]])],"derivedFrom":subQ1}),1.0]])]});}
            var Q77;
            Q77=makeQuery(id+"F2.imprint","IMPRINT",FACE,{"disambiguationData":[TD([[makeQuery(id+"F2.imprint","IMPRINT",EDGE,{"derivedFrom":sQuery(id+"F2.wireOp",EDGE,"E21.16.0")}),1.0]])]});
            var Q78;
            {var subQ0=sQuery(id+"F2.wireOp",EDGE,"E24.17.0");var subQ1=sQuery(id+"F2.wireOp",EDGE,"E22");var subQ2=makeQuery(id+"F2.imprint","INTERSECT",VERTEX,{"disambiguationData":[OD(0.0)],"derivedFrom":[subQ1,subQ0]});Q78=makeQuery(id+"F2.imprint","IMPRINT",FACE,{"disambiguationData":[TD([[makeQuery(id+"F2.imprint","IMPRINT",EDGE,{"disambiguationData":[TD([[subQ2,-1.0]])],"derivedFrom":subQ1}),-1.0]])]});}
            var Q79;
            {var subQ0=sQuery(id+"F2.wireOp",EDGE,"E24.14.0");var subQ1=sQuery(id+"F2.wireOp",EDGE,"E22");var subQ2=makeQuery(id+"F2.imprint","INTERSECT",VERTEX,{"disambiguationData":[OD(0.0)],"derivedFrom":[subQ1,subQ0]});Q79=makeQuery(id+"F2.imprint","IMPRINT",FACE,{"disambiguationData":[TD([[makeQuery(id+"F2.imprint","IMPRINT",EDGE,{"disambiguationData":[TD([[subQ2,-1.0]])],"derivedFrom":subQ1}),1.0]])]});}
            var Q80;
            Q80=makeQuery(id+"F2.imprint","IMPRINT",FACE,{"disambiguationData":[TD([[makeQuery(id+"F2.imprint","IMPRINT",EDGE,{"derivedFrom":sQuery(id+"F2.wireOp",EDGE,"E21.18.0")}),1.0]])]});
            var Q81;
            {var subQ0=sQuery(id+"F2.wireOp",EDGE,"E24.7.0");var subQ1=sQuery(id+"F2.wireOp",EDGE,"E22");var subQ2=makeQuery(id+"F2.imprint","INTERSECT",VERTEX,{"disambiguationData":[OD(0.0)],"derivedFrom":[subQ1,subQ0]});Q81=makeQuery(id+"F2.imprint","IMPRINT",FACE,{"disambiguationData":[TD([[makeQuery(id+"F2.imprint","IMPRINT",EDGE,{"disambiguationData":[TD([[subQ2,-1.0]])],"derivedFrom":subQ1}),1.0]])]});}
            var Q82;
            {var subQ0=sQuery(id+"F2.wireOp",EDGE,"E23");var subQ1=sQuery(id+"F2.wireOp",EDGE,"E22");var subQ2=makeQuery(id+"F2.imprint","INTERSECT",VERTEX,{"disambiguationData":[OD(0.0)],"derivedFrom":[subQ1,subQ0]});Q82=makeQuery(id+"F2.imprint","IMPRINT",FACE,{"disambiguationData":[TD([[makeQuery(id+"F2.imprint","IMPRINT",EDGE,{"disambiguationData":[TD([[subQ2,-1.0]])],"derivedFrom":subQ1}),-1.0]])]});}
            var Q83;
            {var subQ0=sQuery(id+"F2.wireOp",EDGE,"E24.16.0");var subQ1=sQuery(id+"F2.wireOp",EDGE,"E22");var subQ2=makeQuery(id+"F2.imprint","INTERSECT",VERTEX,{"disambiguationData":[OD(0.0)],"derivedFrom":[subQ1,subQ0]});Q83=makeQuery(id+"F2.imprint","IMPRINT",FACE,{"disambiguationData":[TD([[makeQuery(id+"F2.imprint","IMPRINT",EDGE,{"disambiguationData":[TD([[subQ2,-1.0]])],"derivedFrom":subQ1}),1.0]])]});}
            var Q84;
            Q84=makeQuery(id+"F2.imprint","IMPRINT",FACE,{"disambiguationData":[TD([[makeQuery(id+"F2.imprint","IMPRINT",EDGE,{"derivedFrom":sQuery(id+"F2.wireOp",EDGE,"E17.1.21.0")}),1.0]])]});
            var Q85;
            Q85=makeQuery(id+"F2.imprint","IMPRINT",FACE,{"disambiguationData":[TD([[makeQuery(id+"F2.imprint","IMPRINT",EDGE,{"derivedFrom":sQuery(id+"F2.wireOp",EDGE,"E19.1.27.0")}),1.0]])]});
            var Q86;
            {var subQ0=sQuery(id+"F2.wireOp",EDGE,"E24.16.0");var subQ1=sQuery(id+"F2.wireOp",EDGE,"E22");var subQ2=makeQuery(id+"F2.imprint","INTERSECT",VERTEX,{"disambiguationData":[OD(0.0)],"derivedFrom":[subQ1,subQ0]});Q86=makeQuery(id+"F2.imprint","IMPRINT",FACE,{"disambiguationData":[TD([[makeQuery(id+"F2.imprint","IMPRINT",EDGE,{"disambiguationData":[TD([[subQ2,-1.0]])],"derivedFrom":subQ1}),-1.0]])]});}
            var Q87;
            {var subQ0=sQuery(id+"F2.wireOp",EDGE,"E24.13.0");var subQ1=sQuery(id+"F2.wireOp",EDGE,"E22");var subQ2=makeQuery(id+"F2.imprint","INTERSECT",VERTEX,{"disambiguationData":[OD(0.0)],"derivedFrom":[subQ1,subQ0]});Q87=makeQuery(id+"F2.imprint","IMPRINT",FACE,{"disambiguationData":[TD([[makeQuery(id+"F2.imprint","IMPRINT",EDGE,{"disambiguationData":[TD([[subQ2,-1.0]])],"derivedFrom":subQ1}),1.0]])]});}
            extrude(context, id + "F3", {"entities" : qUnion([Q0, Q1, Q2, Q3, Q4, Q5, Q6, Q7, Q8, Q9, Q10, Q11, Q12, Q13, Q14, Q15, Q16, Q17, Q18, Q19, Q20, Q21, Q22, Q23, Q24, Q25, Q26, Q27, Q28, Q29, Q30, Q31, Q32, Q33, Q34, Q35, Q36, Q37, Q38, Q39, Q40, Q41, Q42, Q43, Q44, Q45, Q46, Q47, Q48, Q49, Q50, Q51, Q52, Q53, Q54, Q55, Q56, Q57, Q58, Q59, Q60, Q61, Q62, Q63, Q64, Q65, Q66, Q67, Q68, Q69, Q70, Q71, Q72, Q73, Q74, Q75, Q76, Q77, Q78, Q79, Q80, Q81, Q82, Q83, Q84, Q85, Q86, Q87]), "operationType" : NewBodyOperationType.REMOVE, "endBound" : BoundingType.UP_TO_NEXT, "depth" : 25 * mm});
        }
    });
